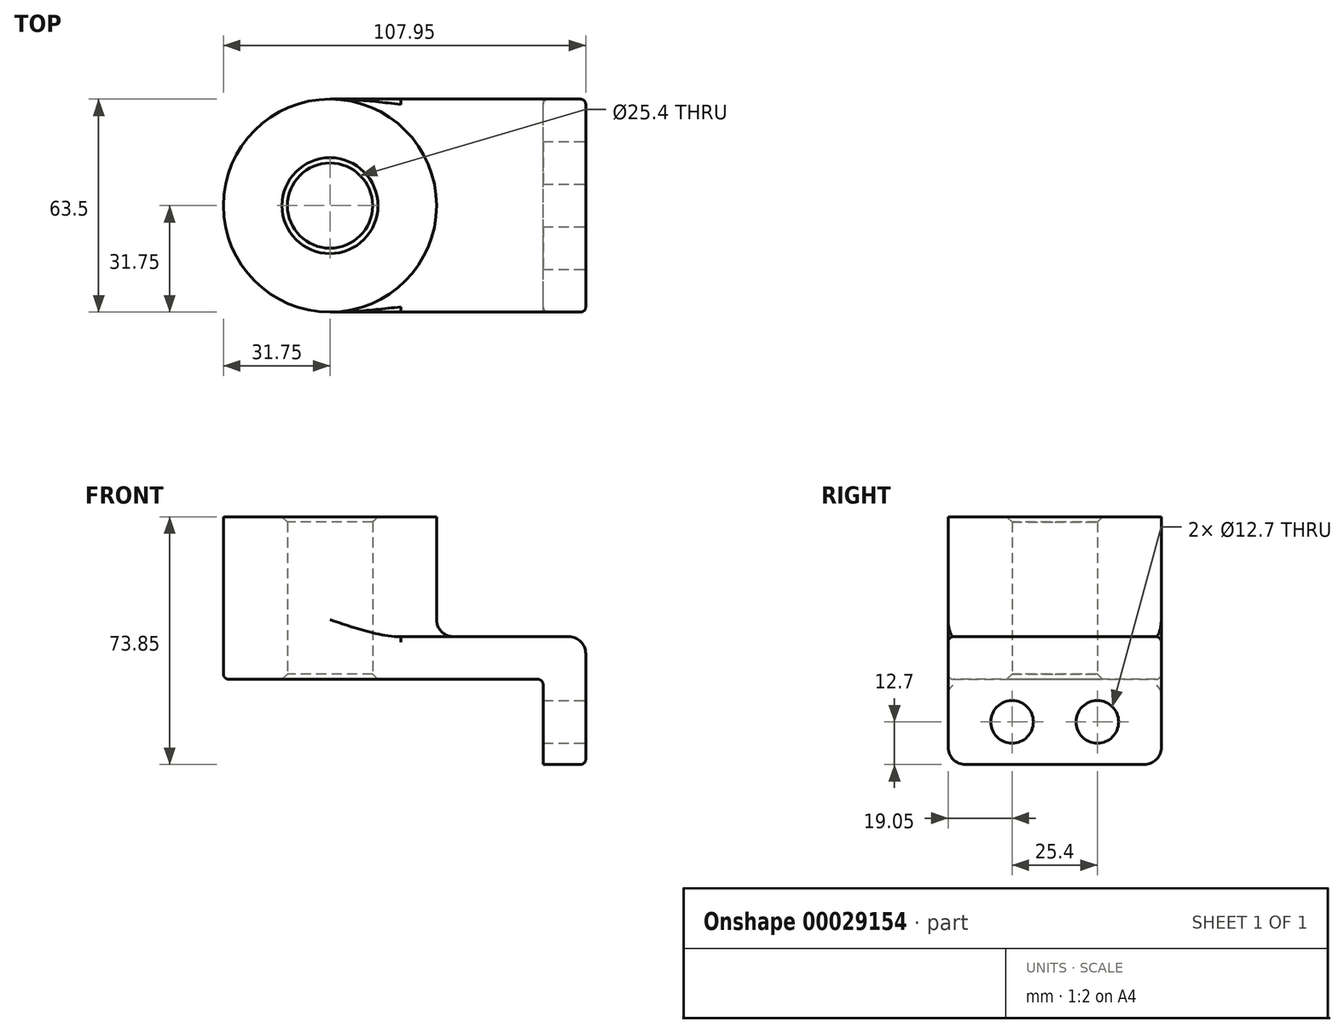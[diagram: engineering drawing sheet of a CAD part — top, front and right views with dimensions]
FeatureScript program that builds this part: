
annotation { "Feature Type Name" : "Feature", "Feature Type Description" : "" }
export const myFeature = defineFeature(function(context is Context, id is Id, definition is map)
    precondition{}
    {
        {
            var Q0;
            Q0=qCreatedBy(makeId("Top.planeOp"),FACE);
            var sketch = newSketch(context, id + "F0", { "sketchPlane" : qUnion([Q0])});
            skLineSegment(sketch, "E0.rect.bottom", {"start": v(-38.1, 31.75) * mm, "end": v(38.1, 31.75) * mm});
            skLineSegment(sketch, "E0.rect.top", {"start": v(-38.1, -31.75) * mm, "end": v(38.1, -31.75) * mm});
            skLineSegment(sketch, "E0.rect.left", {"start": v(-38.1, 31.75) * mm, "end": v(-38.1, -31.75) * mm});
            skLineSegment(sketch, "E0.rect.right", {"start": v(38.1, 31.75) * mm, "end": v(38.1, -31.75) * mm});
            skPoint(sketch, "E0.rect.middle", {"position": v(0, 0) * mm});
            skCircle(sketch, "E1", {"center": v(-38.1, 0) * mm, "radius": 31.75 * mm});
            skCircle(sketch, "E2", {"center": v(-38.1, 0) * mm, "radius": 12.7 * mm});
            skSolve(sketch);
        }
        {
            var Q0;
            Q0 = qSketchRegion(id + "F0", true);
            extrude(context, id + "F1", {"entities" : qUnion([Q0]), "depth" : 12.7 * mm});
        }
        {
            var Q0;
            {var subQ0=sQuery(id+"F0.wireOp",EDGE,"E2");var subQ1=sQuery(id+"F0.wireOp",EDGE,"E0.rect.left");var subQ3=makeQuery(id+"F0.imprint","INTERSECT",VERTEX,{"disambiguationData":[OD(0.0)],"derivedFrom":[subQ1,subQ0]});Q0=makeQuery(id+"F0.imprint","IMPRINT",FACE,{"disambiguationData":[TD([[makeQuery(id+"F0.imprint","IMPRINT",EDGE,{"disambiguationData":[TD([[subQ3,-1.0]])],"derivedFrom":subQ0}),-1.0]])]});}
            var Q1;
            {var subQ0=sQuery(id+"F0.wireOp",EDGE,"E2");var subQ1=sQuery(id+"F0.wireOp",EDGE,"E0.rect.left");var subQ3=makeQuery(id+"F0.imprint","INTERSECT",VERTEX,{"disambiguationData":[OD(0.0)],"derivedFrom":[subQ1,subQ0]});Q1=makeQuery(id+"F0.imprint","IMPRINT",FACE,{"disambiguationData":[TD([[makeQuery(id+"F0.imprint","IMPRINT",EDGE,{"disambiguationData":[TD([[subQ3,1.0]])],"derivedFrom":subQ0}),-1.0]])]});}
            extrude(context, id + "F2", {"entities" : qUnion([Q0, Q1]), "operationType" : NewBodyOperationType.ADD, "depth" : 48.45 * mm});
        }
        {
            var Q0;
            Q0=makeQuery(id+"F1.opExtrude","SWEPT_FACE",FACE,{"disambiguationData":[OSD([sQuery(id+"F0.wireOp",EDGE,"E0.rect.right")])]});
            var sketch = newSketch(context, id + "F3", { "sketchPlane" : qUnion([Q0])});
            skLineSegment(sketch, "E3.bottom", {"start": v(-31.75, 12.7) * mm, "end": v(31.75, 12.7) * mm});
            skLineSegment(sketch, "E3.top", {"start": v(-31.75, -25.4) * mm, "end": v(31.75, -25.4) * mm});
            skLineSegment(sketch, "E3.left", {"start": v(-31.75, 12.7) * mm, "end": v(-31.75, -25.4) * mm});
            skLineSegment(sketch, "E3.right", {"start": v(31.75, 12.7) * mm, "end": v(31.75, -25.4) * mm});
            skLineSegment(sketch, "E4", {"start": v(0, 0) * mm, "end": v(0, -25.4) * mm, "construction": true});
            skCircle(sketch, "E5", {"center": v(-12.7, -12.7) * mm, "radius": 6.35 * mm});
            skCircle(sketch, "E6.MirrorC", {"center": v(12.7, -12.7) * mm, "radius": 6.35 * mm});
            skSolve(sketch);
        }
        {
            var Q0;
            {var subQ2=sQuery(id+"F3.wireOp",EDGE,"E3.top");Q0=makeQuery(id+"F3.imprint","IMPRINT",FACE,{"disambiguationData":[TD([[makeQuery(id+"F3.imprint","IMPRINT",EDGE,{"derivedFrom":subQ2}),1.0]])]});}
            var Q1;
            {var subQ2=sQuery(id+"F3.wireOp",EDGE,"E3.bottom");Q1=makeQuery(id+"F3.imprint","IMPRINT",FACE,{"disambiguationData":[TD([[makeQuery(id+"F3.imprint","IMPRINT",EDGE,{"derivedFrom":subQ2}),1.0]])]});}
            extrude(context, id + "F4", {"entities" : qUnion([Q0, Q1]), "operationType" : NewBodyOperationType.ADD, "oppositeDirection" : true, "depth" : 12.7 * mm});
        }
        {
            var Q0;
            {var subQ0=sQuery(id+"F0.wireOp",EDGE,"E1");Q0=makeQuery(id+"F2.boolean.opBoolean","INTERSECT",EDGE,{"derivedFrom":[makeQuery(id+"F1.opExtrude","CAP_FACE",FACE,{"disambiguationData":[OSD([sQuery(id+"F0.wireOp",EDGE,"E0.rect.bottom"),sQuery(id+"F0.wireOp",EDGE,"E0.rect.top"),sQuery(id+"F0.wireOp",EDGE,"E0.rect.right"),subQ0,sQuery(id+"F0.wireOp",EDGE,"E2")])],"isStart":false}),makeQuery(id+"F2.opExtrude","SWEPT_FACE",FACE,{"disambiguationData":[OSD([subQ0])]})]});}
            var Q1;
            Q1=makeQuery(id+"F1.opExtrude","CAP_EDGE",EDGE,{"disambiguationData":[OSD([sQuery(id+"F0.wireOp",EDGE,"E0.rect.right")])],"isStart":false});
            var Q2;
            Q2=makeQuery(id+"F4.opExtrude","SWEPT_EDGE",EDGE,{"disambiguationData":[OSD([sQuery(id+"F3.wireOp",EDGE,"E3.top"),sQuery(id+"F3.wireOp",EDGE,"E3.left")])]});
            var Q3;
            Q3=makeQuery(id+"F4.opExtrude","SWEPT_EDGE",EDGE,{"disambiguationData":[OSD([sQuery(id+"F3.wireOp",EDGE,"E3.top"),sQuery(id+"F3.wireOp",EDGE,"E3.right")])]});
            fillet(context, id + "F5", {"entities" : qUnion([Q0, Q1, Q2, Q3]), "radius" : 5.08 * mm, "tangentPropagation" : true, "allowEdgeOverflow" : false});
        }
        {
            var Q0;
            Q0=makeQuery(id+"F1.opExtrude","CAP_EDGE",EDGE,{"disambiguationData":[OSD([sQuery(id+"F0.wireOp",EDGE,"E0.rect.top")])],"isStart":false});
            var Q1;
            Q1=makeQuery(id+"F1.opExtrude","CAP_EDGE",EDGE,{"disambiguationData":[OSD([sQuery(id+"F0.wireOp",EDGE,"E0.rect.top")])],"isStart":true});
            var Q2;
            Q2=makeQuery(id+"F4.boolean.opBoolean","INTERSECT",EDGE,{"derivedFrom":[makeQuery(id+"F1.opExtrude","CAP_FACE",FACE,{"disambiguationData":[OSD([sQuery(id+"F0.wireOp",EDGE,"E0.rect.bottom"),sQuery(id+"F0.wireOp",EDGE,"E0.rect.top"),sQuery(id+"F0.wireOp",EDGE,"E0.rect.right"),sQuery(id+"F0.wireOp",EDGE,"E1"),sQuery(id+"F0.wireOp",EDGE,"E2")])],"isStart":true}),makeQuery(id+"F4.opExtrude","CAP_FACE",FACE,{"disambiguationData":[OSD([sQuery(id+"F3.wireOp",EDGE,"E3.bottom"),sQuery(id+"F3.wireOp",EDGE,"E3.top"),sQuery(id+"F3.wireOp",EDGE,"E3.left"),sQuery(id+"F3.wireOp",EDGE,"E3.right"),sQuery(id+"F3.wireOp",EDGE,"E5"),sQuery(id+"F3.wireOp",EDGE,"E6.MirrorC")])],"isStart":false})]});
            fillet(context, id + "F6", {"entities" : qUnion([Q0, Q1, Q2]), "radius" : 1.59 * mm, "tangentPropagation" : true, "allowEdgeOverflow" : false});
        }
        {
            var Q0;
            {var subQ0=sQuery(id+"F0.wireOp",EDGE,"E2");Q0=makeQuery(id+"F2.boolean.opBoolean","MERGE",FACE,{"derivedFrom":[makeQuery(id+"F1.opExtrude","SWEPT_FACE",FACE,{"disambiguationData":[OSD([subQ0])]}),makeQuery(id+"F2.opExtrude","SWEPT_FACE",FACE,{"disambiguationData":[OSD([subQ0])]})]});}
            chamfer(context, id + "F7", {"entities" : qUnion([Q0]), "width" : 1.59 * mm, "tangentPropagation" : true});
        }
    });
